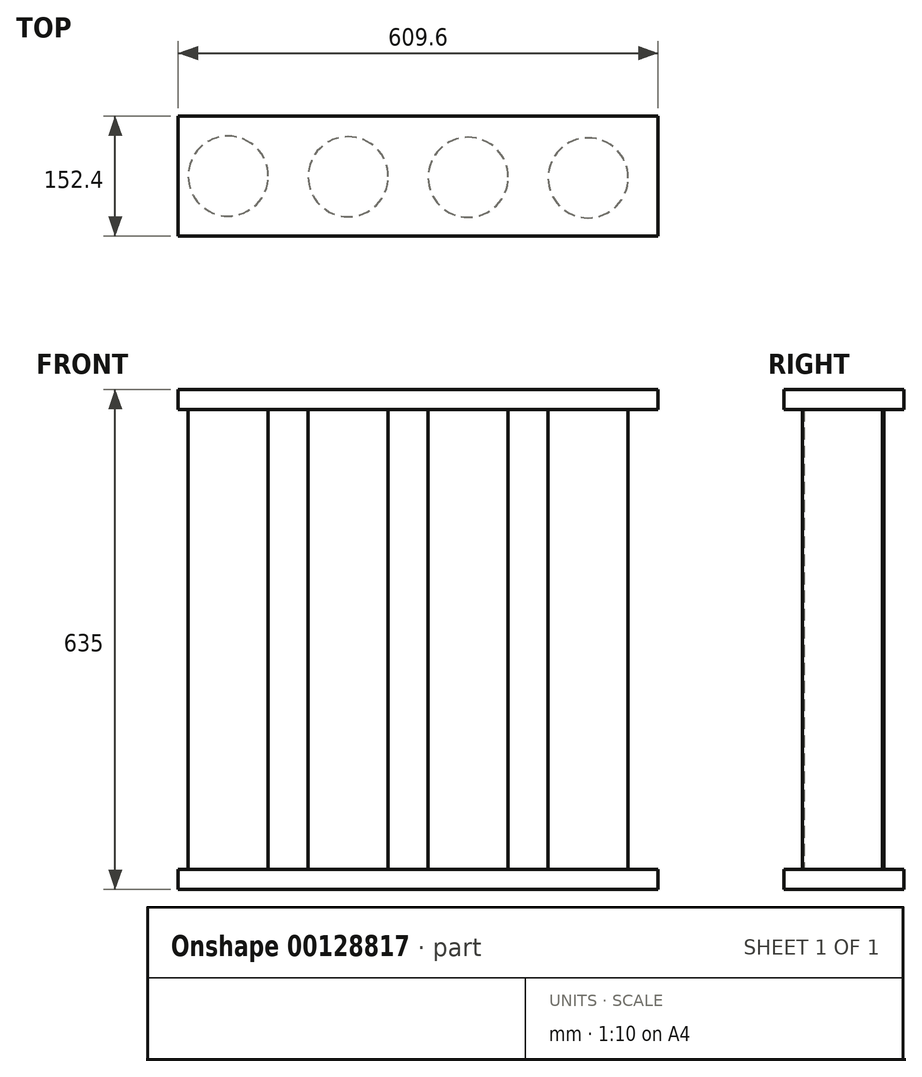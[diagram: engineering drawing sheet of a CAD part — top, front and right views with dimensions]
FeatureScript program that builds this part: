
annotation { "Feature Type Name" : "Feature", "Feature Type Description" : "" }
export const myFeature = defineFeature(function(context is Context, id is Id, definition is map)
    precondition{}
    {
        {
            var Q0;
            Q0=qCreatedBy(makeId("Top.planeOp"),FACE);
            var sketch = newSketch(context, id + "F0", { "sketchPlane" : qUnion([Q0])});
            skLineSegment(sketch, "E0.bottom", {"start": v(-305.15, 114.33) * mm, "end": v(304.45, 114.33) * mm});
            skLineSegment(sketch, "E0.top", {"start": v(-305.15, -38.07) * mm, "end": v(304.45, -38.07) * mm});
            skLineSegment(sketch, "E0.left", {"start": v(-305.15, 114.33) * mm, "end": v(-305.15, -38.07) * mm});
            skLineSegment(sketch, "E0.right", {"start": v(304.45, 114.33) * mm, "end": v(304.45, -38.07) * mm});
            skSolve(sketch);
        }
        {
            var Q0;
            Q0=makeQuery(id+"F0.imprint","IMPRINT",FACE,{"disambiguationData":[TD([[makeQuery(id+"F0.imprint","IMPRINT",EDGE,{"derivedFrom":sQuery(id+"F0.wireOp",EDGE,"E0.bottom")}),-1.0]])]});
            extrude(context, id + "F1", {"entities" : qUnion([Q0]), "depth" : 25.4 * mm});
        }
        {
            var Q0;
            Q0=makeQuery(id+"F1.opExtrude","CAP_FACE",FACE,{"disambiguationData":[OSD([sQuery(id+"F0.wireOp",EDGE,"E0.bottom"),sQuery(id+"F0.wireOp",EDGE,"E0.top"),sQuery(id+"F0.wireOp",EDGE,"E0.left"),sQuery(id+"F0.wireOp",EDGE,"E0.right")])],"isStart":false});
            var sketch = newSketch(context, id + "F2", { "sketchPlane" : qUnion([Q0])});
            skCircle(sketch, "E1", {"center": v(-241.65, 38.13) * mm, "radius": 50.8 * mm});
            skCircle(sketch, "E2.1.0.0", {"center": v(-89.25, 37.36) * mm, "radius": 50.8 * mm});
            skCircle(sketch, "E2.2.0.0", {"center": v(63.15, 36.6) * mm, "radius": 50.8 * mm});
            skCircle(sketch, "E2.3.0.0", {"center": v(215.54, 35.83) * mm, "radius": 50.8 * mm});
            skLineSegment(sketch, "E2.direction1", {"start": v(-241.65, 38.13) * mm, "end": v(-89.25, 37.36) * mm, "construction": true});
            skSolve(sketch);
        }
        {
            var Q0;
            Q0=makeQuery(id+"F2.imprint","IMPRINT",FACE,{"disambiguationData":[TD([[makeQuery(id+"F2.imprint","IMPRINT",EDGE,{"derivedFrom":sQuery(id+"F2.wireOp",EDGE,"E2.3.0.0")}),1.0]])]});
            var Q1;
            Q1=makeQuery(id+"F2.imprint","IMPRINT",FACE,{"disambiguationData":[TD([[makeQuery(id+"F2.imprint","IMPRINT",EDGE,{"derivedFrom":sQuery(id+"F2.wireOp",EDGE,"E2.2.0.0")}),1.0]])]});
            var Q2;
            Q2=makeQuery(id+"F2.imprint","IMPRINT",FACE,{"disambiguationData":[TD([[makeQuery(id+"F2.imprint","IMPRINT",EDGE,{"derivedFrom":sQuery(id+"F2.wireOp",EDGE,"E2.1.0.0")}),1.0]])]});
            var Q3;
            Q3=makeQuery(id+"F2.imprint","IMPRINT",FACE,{"disambiguationData":[TD([[makeQuery(id+"F2.imprint","IMPRINT",EDGE,{"derivedFrom":sQuery(id+"F2.wireOp",EDGE,"E1")}),1.0]])]});
            extrude(context, id + "F3", {"entities" : qUnion([Q0, Q1, Q2, Q3]), "operationType" : NewBodyOperationType.ADD, "depth" : 609.6 * mm});
        }
        {
            var Q0;
            Q0=makeQuery(id+"F3.opExtrude","CAP_FACE",FACE,{"disambiguationData":[OSD([sQuery(id+"F2.wireOp",EDGE,"E1")])],"isStart":false});
            var sketch = newSketch(context, id + "F4", { "sketchPlane" : qUnion([Q0])});
            skLineSegment(sketch, "E3.bottom", {"start": v(-305.15, 114.33) * mm, "end": v(304.45, 114.33) * mm});
            skLineSegment(sketch, "E3.top", {"start": v(-305.15, -38.07) * mm, "end": v(304.45, -38.07) * mm});
            skLineSegment(sketch, "E3.left", {"start": v(-305.15, 114.33) * mm, "end": v(-305.15, -38.07) * mm});
            skLineSegment(sketch, "E3.right", {"start": v(304.45, 114.33) * mm, "end": v(304.45, -38.07) * mm});
            skSolve(sketch);
        }
        {
            var Q0;
            Q0=makeQuery(id+"F4.imprint","IMPRINT",FACE,{"disambiguationData":[TD([[makeQuery(id+"F4.imprint","IMPRINT",EDGE,{"derivedFrom":sQuery(id+"F4.wireOp",EDGE,"E3.bottom")}),-1.0]])]});
            extrude(context, id + "F5", {"entities" : qUnion([Q0]), "operationType" : NewBodyOperationType.ADD, "oppositeDirection" : true, "depth" : 25.4 * mm});
        }
    });
